# Revit family: BATHTUB (397)
name_source: partatom
category: Plumbing Fixtures
units: mm (PartAtom-declared; Revit-internal decimal feet)

## family parameters
Cut with Voids When Loaded = No
Host = Face
OmniClass Number = 23.45.05.14.21.11
OmniClass Title = Bath/Shower Units
Part Type = Normal
Room Calculation Point = No
Round Connector Dimension = Use Radius
Shared = No

## types (1)
- Cast_Acrylic-Honed_White-HW1
    ADA Compliant = No
    Assembly Code = D2010510
    Default Elevation = 0' - 0"
    Description = Abrazo(TM) freestanding bath
    Finish = Cast_Acrylic-Kohler-HW1-Honed_White
    Height = 2' - 4 1/2"
    Length = 2' - 7 1/2"
    Manufacturer = Kohler
    Model = K-1800
    Product Documentation Link = http://www.us.kohler.com
    Product Page URL = http://www.us.kohler.com
    Sanitary Connector = Sanitary Connection
    Sanitary Diameter = 2"
    Sanitary Radius = 1"
    URL = http://www.us.kohler.com
    WFU = 0
    Waste Connection = Yes
    Width = 5' - 6"

## geometry (parser evidence)
native form markers: Sweep x2
no freeform markers — native parametric forms only
